# Revit family: Spot 4.4
name_source: partatom
category: Lighting Fixtures
units: mm (PartAtom-declared; Revit-internal decimal feet)

## family parameters
Always vertical = No
Cut with Voids When Loaded = No
Light Source = No
OmniClass Number = 23.80.70.00
OmniClass Title = Lighting
Part Type = Normal
Room Calculation Point = Yes
Round Connector Dimension = Use Diameter
Shared = No
Work Plane-Based = Yes

## types (4) — shared parameters
Apparent Load Phase 1 = 5 W
Body = L&L_Anticorodal aluminium
Braket = L&L_aluminium
Code = -
Control system = ON/OFF
Cutout dimensions = -
Default Elevation = 1219 mm
Delivered lumen output = 1923 lm (3000K, 15°, 22W), 2450 lm (3000K, 15°, 32W)
Description = projector for outdoor applications
Energy efficiency class = A A+ A++
Features = -
H1 = 100 mm  [stored 0.328084 ft]
Height mm = 210 mm
Horizontal rotation max = 205.00°
Horizontal rotation min = 52.00°
IP = IP66
LED Colour = 2700K, 3000K, 4000K
Length mm = 179 mm
Lens = L&L_Tempered extra-clear glass
Lumen output at source = 2365 lm (3000K, 22W), 3010 lm (3000K, 32W)
Manufacturer = L&L Luce&Light
Material = body in anticorodal aluminium, bracket in aluminium, screen in serigraphed, tempered, transparent extra-clear glass
Model = Spot 4.4
Mounting = surface mounted (ceiling, wall, ground, spike)
No. and type of led = 1 COB LED, 2-step MacAdam, 50 000h L90 B10 (Ta 25°C)
Notes = version with honeycomb louvre available on request
Power = 22W / 32W
Power cables = includes 1.50 m neoprene cable H05RN-F 3x1,0 Ø7 mm
Power supply = 230Vac
Power supply unit = built-in
Trim = Luce&Light_Black Aluminum
URL = https://www.lucelight.it
URL Accessories and power supply units = https://www.lucelight.it
URL DXF = https://www.lucelight.it
URL Description = https://www.lucelight.it
URL General code = https://www.lucelight.it
URL IES Photometric file = https://www.lucelight.it
URL Image = https://www.lucelight.it
Vertical rotation max = 360.00°
Weight kg = 2.50 kg
Width mm = 109 mm
Wiring = -
X1 = 125 mm  [stored 0.410105 ft]

## per-type parameters (varying)
| type | Geometry | Light Source Spot 4.4 | Optics |
| Spot 4.4 S 15° (3000K 32W 230Vac) | Spot 4.4 movable | Spot 4.4_light source : S 15° | 15° |
| Spot 4.4 M 24° (3000K 32W 230Vac) | Spot 4.4_Braket | Spot 4.4_light source : M 24° | 24° |
| Spot 4.4 L 32° (3000K 32W 230Vac) | Spot 4.4_Braket | Spot 4.4_light source : L 32° | 32° |
| Spot 4.4 J 54° (3000K 32W 230Vac) | Spot 4.4_Braket | Spot 4.4_light source : J 54° | 54° |

note: [stored X ft] marks values corroborated as IEEE doubles in the binary element streams (Revit-internal decimal feet)

## geometry (parser evidence)
native form markers: Blend x6, Sweep x20
no freeform markers — native parametric forms only
